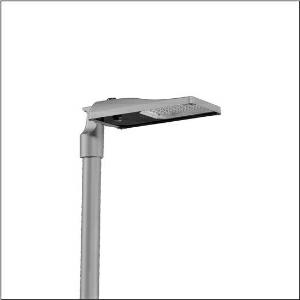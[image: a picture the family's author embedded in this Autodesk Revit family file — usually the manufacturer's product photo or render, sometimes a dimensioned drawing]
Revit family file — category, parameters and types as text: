
# Revit family: streetlight_sl_31_mini___p0_8a_5xh6u31t08ja_d345
name_source: partatom
category: Lighting Fixtures
units: mm (PartAtom-declared; Revit-internal decimal feet)

## family parameters
Cut with Voids When Loaded = No
Host = Face
Light Source = No
Part Type = Normal
Room Calculation Point = No
Round Connector Dimension = Use Diameter
Shared = No

## types (1)
- --- (1 x LED, 12370 lm, 82.5 W, 3000K)
    Apparent Load = 83 VA
    CIE Flux Codes = 36 69 97 100 100
    Color Rendering = 70
    Color Temperature = 3000K
    Default Elevation = 1800 mm
    Description = Streetlight SL 31 mini D4i, Desk-Remote mast luminaire for post-top, side-entry; light control with lens of PMMA; light distribution: P0.8a, direct asymmetric distribution, for standard-compliant lighting for roads and squares; LED: luminous flux: 12.370lm, light colour: 730, colour temperature: 3000K; luminous efficacy: 149,9lm/W; control: pre-setting: logarithmic dimming characteristic, flexible luminous flux parameterisation, time-dependent luminous flux control, constant luminous flux control, power reduction, intelligent temperature release in ECG and LED module, overheat protection; luminaire housing, of diecast aluminium, SITECO metallic grey (DB 702S), corrosivity category C5 high according to DIN EN ISO 12944; cover of toughened safety glass, transparent, opened without tools; mast flange of diecast aluminium, SITECO metallic grey (DB 702S), spigot size: 76/60mm, mast flange included unmounted; cable length: 10,5m, connection cable pre-assembled; mains connection: 220..240V, AC, 50/60Hz; power consumption (at start of service life): 82,5W / (at end of service life): 90,1W / (with reduced operation 50%): 36,8W; protection rating (complete): IP66; insulation class (complete): insulation class II (safety insulation); impact resistance: IK09; certification: CE, ENEC, ENEC+, VDE, UKCA, ZD4i; permissible operating ambient temperature for outdoor applications: -40..+50°C; packaging unit: 1 piece

Light Distribution: P0.8a
    Height = 76 mm
    Lamp = 1 x LED
    Lamp Light Flux = 12370 lm
    Lamp Power = 82.5 W
    Lamp count = 1
    Length = 547 mm
    Luminous efficacy = 150 lm/W
    Manufacturer = Siteco
    ModVariant = No
    Model = 5XH6U31T08JA
    Number of Poles = 1
    OnlyDefault = Yes
    Power Factor = 1
    Product Name = Streetlight SL 31 mini | P0.8a
    Product group = mast luminaire | pylon top
    ProductGroupID = 6100
    Protection Class = Protection class II
    Protection Degree = IP 66
    RLX_Detail_Level = 1
    RLX_Emergency_Light_Flux = 0 lm
    RLX_Emergency_Type = 0
    RLX_Emergency_Type_DB = No
    RlxData = <blob elided: 39561 chars, md5=73874e08>
    Socket = socket
    Standby Power = 0 W
    System Light Flux = 12370 lm
    System Power = 83 W
    Type Comments = factory setting: luminous flux: 100 % | dim-lin: 254 | 870 mA
    Type Image = l_1300332.jpg
    URL = http://relux.com
    VarID = @adj_065115
    Voltage = 0 V
    Weight = 0.00 kg
    Width = 265 mm

## geometry (parser evidence)
native form markers: Blend x4, Sweep x8
no freeform markers — native parametric forms only
